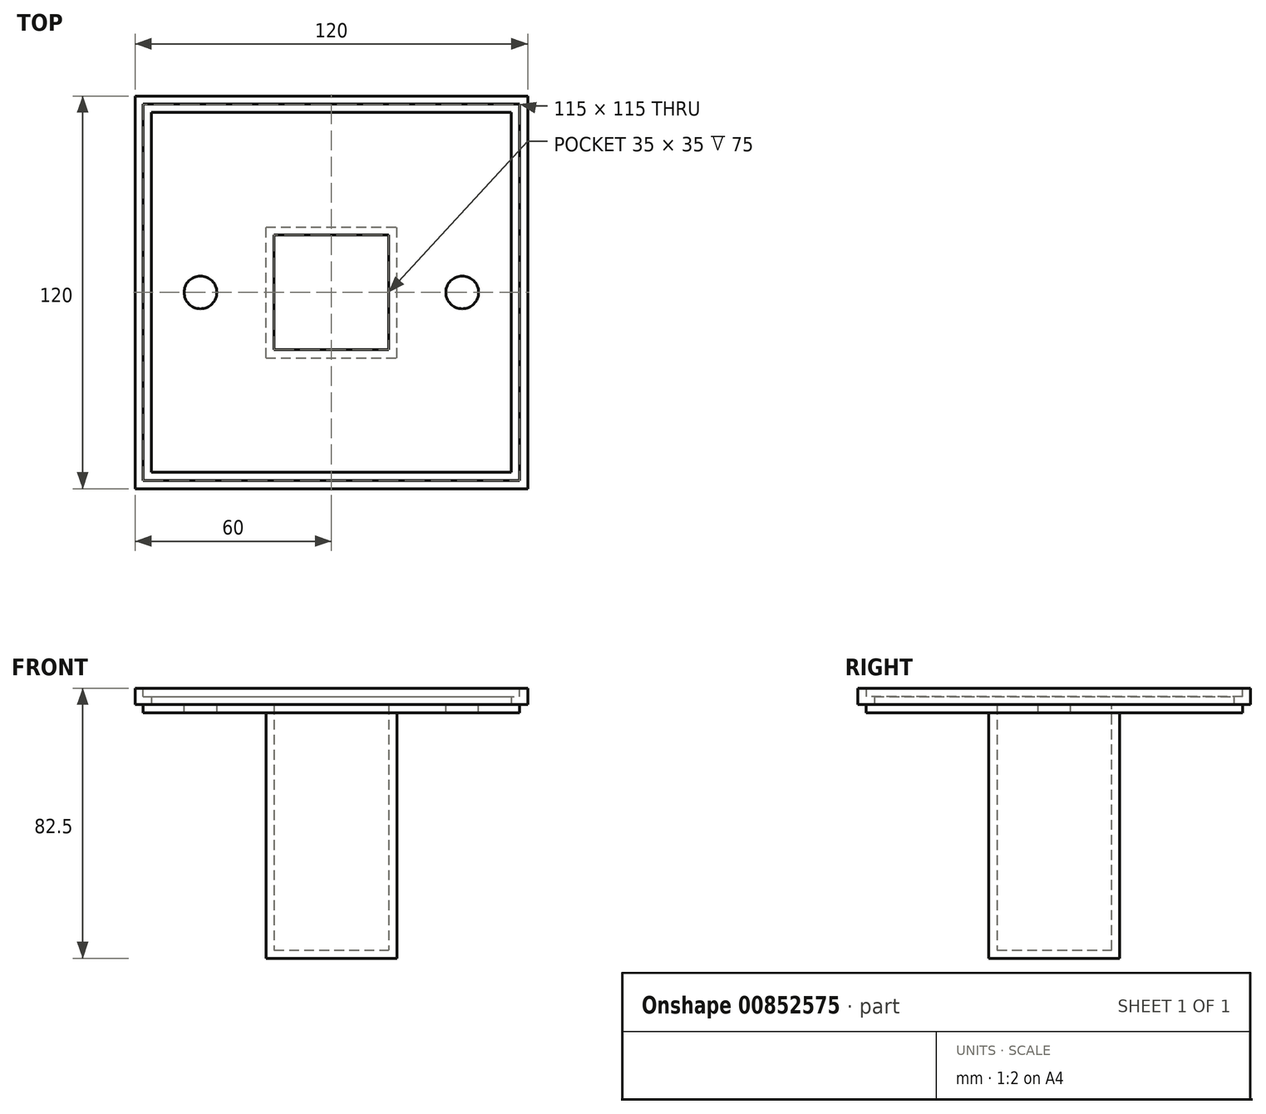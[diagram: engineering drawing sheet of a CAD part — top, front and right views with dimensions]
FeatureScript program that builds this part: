
annotation { "Feature Type Name" : "Feature", "Feature Type Description" : "" }
export const myFeature = defineFeature(function(context is Context, id is Id, definition is map)
    precondition{}
    {
        {
            var Q0;
            Q0=qCreatedBy(makeId("Top.planeOp"),FACE);
            cPlane(context, id + "F0", {"entities" : qUnion([Q0]), "cplaneType" : CPlaneType.OFFSET, "offset" : 75 * mm, "oppositeDirection" : true, "width" : 150 * mm, "height" : 150 * mm});
        }
        {
            var Q0;
            Q0=qCreatedBy(id+"F0.planeOp",FACE);
            var sketch = newSketch(context, id + "F1", { "sketchPlane" : qUnion([Q0])});
            skLineSegment(sketch, "E0.bottom", {"start": v(-20, -20) * mm, "end": v(20, -20) * mm});
            skLineSegment(sketch, "E0.top", {"start": v(-20, 20) * mm, "end": v(20, 20) * mm});
            skLineSegment(sketch, "E0.left", {"start": v(-20, -20) * mm, "end": v(-20, 20) * mm});
            skLineSegment(sketch, "E0.right", {"start": v(20, -20) * mm, "end": v(20, 20) * mm});
            skPoint(sketch, "E0.middle", {"position": v(0, 0) * mm});
            skSolve(sketch);
        }
        {
            var Q0;
            Q0=qCreatedBy(makeId("Top.planeOp"),FACE);
            cPlane(context, id + "F2", {"entities" : qUnion([Q0]), "cplaneType" : CPlaneType.OFFSET, "offset" : 2.5 * mm, "width" : 150 * mm, "height" : 150 * mm});
        }
        {
            var Q0;
            Q0=qCreatedBy(id+"F2.planeOp",FACE);
            cPlane(context, id + "F3", {"entities" : qUnion([Q0]), "cplaneType" : CPlaneType.OFFSET, "offset" : 2.5 * mm, "width" : 150 * mm, "height" : 150 * mm});
        }
        {
            var Q0;
            Q0=qCreatedBy(makeId("Top.planeOp"),FACE);
            var sketch = newSketch(context, id + "F4", { "sketchPlane" : qUnion([Q0])});
            skLineSegment(sketch, "E1.bottom", {"start": v(-57.5, -57.5) * mm, "end": v(57.5, -57.5) * mm});
            skLineSegment(sketch, "E1.top", {"start": v(-57.5, 57.5) * mm, "end": v(57.5, 57.5) * mm});
            skLineSegment(sketch, "E1.left", {"start": v(-57.5, -57.5) * mm, "end": v(-57.5, 57.5) * mm});
            skLineSegment(sketch, "E1.right", {"start": v(57.5, -57.5) * mm, "end": v(57.5, 57.5) * mm});
            skPoint(sketch, "E1.middle", {"position": v(0, 0) * mm});
            skSolve(sketch);
        }
        {
            var Q0;
            Q0=qCreatedBy(id+"F2.planeOp",FACE);
            var sketch = newSketch(context, id + "F5", { "sketchPlane" : qUnion([Q0])});
            skLineSegment(sketch, "E2.bottom", {"start": v(-57.5, -57.5) * mm, "end": v(57.5, -57.5) * mm});
            skLineSegment(sketch, "E2.top", {"start": v(-57.5, 57.5) * mm, "end": v(57.5, 57.5) * mm});
            skLineSegment(sketch, "E2.left", {"start": v(-57.5, -57.5) * mm, "end": v(-57.5, 57.5) * mm});
            skLineSegment(sketch, "E2.right", {"start": v(57.5, -57.5) * mm, "end": v(57.5, 57.5) * mm});
            skPoint(sketch, "E2.middle", {"position": v(0, 0) * mm});
            skSolve(sketch);
        }
        {
            var Q0;
            Q0=qCreatedBy(id+"F3.planeOp",FACE);
            var sketch = newSketch(context, id + "F6", { "sketchPlane" : qUnion([Q0])});
            skLineSegment(sketch, "E3.bottom", {"start": v(-60, 60) * mm, "end": v(60, 60) * mm});
            skLineSegment(sketch, "E3.top", {"start": v(-60, -60) * mm, "end": v(60, -60) * mm});
            skLineSegment(sketch, "E3.left", {"start": v(-60, 60) * mm, "end": v(-60, -60) * mm});
            skLineSegment(sketch, "E3.right", {"start": v(60, 60) * mm, "end": v(60, -60) * mm});
            skPoint(sketch, "E3.middle", {"position": v(0, 0) * mm});
            skSolve(sketch);
        }
        {
            var Q0;
            Q0=qCreatedBy(makeId("Top.planeOp"),FACE);
            var sketch = newSketch(context, id + "F7", { "sketchPlane" : qUnion([Q0])});
            skLineSegment(sketch, "E4.bottom", {"start": v(-20, -20) * mm, "end": v(20, -20) * mm});
            skLineSegment(sketch, "E4.top", {"start": v(-20, 20) * mm, "end": v(20, 20) * mm});
            skLineSegment(sketch, "E4.left", {"start": v(-20, -20) * mm, "end": v(-20, 20) * mm});
            skLineSegment(sketch, "E4.right", {"start": v(20, -20) * mm, "end": v(20, 20) * mm});
            skPoint(sketch, "E4.middle", {"position": v(0, 0) * mm});
            skSolve(sketch);
        }
        {
            var Q0;
            Q0=makeQuery(id+"F1.imprint","IMPRINT",FACE,{"disambiguationData":[TD([[makeQuery(id+"F1.imprint","IMPRINT",EDGE,{"derivedFrom":sQuery(id+"F1.wireOp",EDGE,"E0.bottom")}),1.0]])]});
            var Q1;
            Q1=makeQuery(id+"F7.imprint","IMPRINT",FACE,{"disambiguationData":[TD([[makeQuery(id+"F7.imprint","IMPRINT",EDGE,{"derivedFrom":sQuery(id+"F7.wireOp",EDGE,"E4.bottom")}),1.0]])]});
            loft(context, id + "F8", {"sheetProfilesArray" : [{ "sheetProfileEntities" : qUnion([Q0]) }, { "sheetProfileEntities" : qUnion([Q1]) }]});
        }
        {
            var Q1;
            Q1=makeQuery(id+"F4.imprint","IMPRINT",FACE,{"disambiguationData":[TD([[makeQuery(id+"F4.imprint","IMPRINT",EDGE,{"derivedFrom":sQuery(id+"F4.wireOp",EDGE,"E1.bottom")}),1.0]])]});
            var Q2;
            Q2=makeQuery(id+"F5.imprint","IMPRINT",FACE,{"disambiguationData":[TD([[makeQuery(id+"F5.imprint","IMPRINT",EDGE,{"derivedFrom":sQuery(id+"F5.wireOp",EDGE,"E2.bottom")}),1.0]])]});
            loft(context, id + "F9", {"operationType" : NewBodyOperationType.ADD, "sheetProfilesArray" : [{ "sheetProfileEntities" : qUnion([Q1]) }, { "sheetProfileEntities" : qUnion([Q2]) }]});
        }
        {
            var Q0;
            Q0=qCreatedBy(id+"F2.planeOp",FACE);
            var sketch = newSketch(context, id + "F10", { "sketchPlane" : qUnion([Q0])});
            skLineSegment(sketch, "E5.bottom", {"start": v(-60, 60) * mm, "end": v(60, 60) * mm});
            skLineSegment(sketch, "E5.top", {"start": v(-60, -60) * mm, "end": v(60, -60) * mm});
            skLineSegment(sketch, "E5.left", {"start": v(-60, 60) * mm, "end": v(-60, -60) * mm});
            skLineSegment(sketch, "E5.right", {"start": v(60, 60) * mm, "end": v(60, -60) * mm});
            skPoint(sketch, "E5.middle", {"position": v(0, 0) * mm});
            skSolve(sketch);
        }
        {
            var Q1;
            Q1=makeQuery(id+"F6.imprint","IMPRINT",FACE,{"disambiguationData":[TD([[makeQuery(id+"F6.imprint","IMPRINT",EDGE,{"derivedFrom":sQuery(id+"F6.wireOp",EDGE,"E3.bottom")}),-1.0]])]});
            var Q2;
            Q2=makeQuery(id+"F10.imprint","IMPRINT",FACE,{"disambiguationData":[TD([[makeQuery(id+"F10.imprint","IMPRINT",EDGE,{"derivedFrom":sQuery(id+"F10.wireOp",EDGE,"E5.bottom")}),-1.0]])]});
            loft(context, id + "F11", {"operationType" : NewBodyOperationType.ADD, "sheetProfilesArray" : [{ "sheetProfileEntities" : qUnion([Q1]) }, { "sheetProfileEntities" : qUnion([Q2]) }]});
        }
        {
            var Q0;
            Q0=makeQuery(id+"F11.opLoft","CAP_FACE",FACE,{"disambiguationData":[OSD([makeQuery(id+"F6.imprint","IMPRINT",FACE,{"disambiguationData":[TD([[makeQuery(id+"F6.imprint","IMPRINT",EDGE,{"derivedFrom":sQuery(id+"F6.wireOp",EDGE,"E3.bottom")}),-1.0]])]})])],"isStart":true});
            var sketch = newSketch(context, id + "F12", { "sketchPlane" : qUnion([Q0])});
            skPoint(sketch, "E6", {"position": v(0, 0) * mm});
            skSolve(sketch);
        }
        {
            var Q0;
            Q0=qCreatedBy(id+"F3.planeOp",FACE);
            cPlane(context, id + "F13", {"entities" : qUnion([Q0]), "cplaneType" : CPlaneType.OFFSET, "offset" : 2.5 * mm, "width" : 150 * mm, "height" : 150 * mm});
        }
        {
            var Q0;
            Q0=qCreatedBy(id+"F13.planeOp",FACE);
            var sketch = newSketch(context, id + "F14", { "sketchPlane" : qUnion([Q0])});
            skLineSegment(sketch, "E7.bottom", {"start": v(-60, 60) * mm, "end": v(60, 60) * mm});
            skLineSegment(sketch, "E7.top", {"start": v(-60, -60) * mm, "end": v(60, -60) * mm});
            skLineSegment(sketch, "E7.left", {"start": v(-60, 60) * mm, "end": v(-60, -60) * mm});
            skLineSegment(sketch, "E7.right", {"start": v(60, 60) * mm, "end": v(60, -60) * mm});
            skPoint(sketch, "E7.middle", {"position": v(0, 0) * mm});
            skSolve(sketch);
        }
        {
            var Q1;
            Q1=makeQuery(id+"F14.imprint","IMPRINT",FACE,{"disambiguationData":[TD([[makeQuery(id+"F14.imprint","IMPRINT",EDGE,{"derivedFrom":sQuery(id+"F14.wireOp",EDGE,"E7.bottom")}),-1.0]])]});
            var Q2;
            {var subQ0=sQuery(id+"F6.wireOp",EDGE,"E3.right");var subQ1=sQuery(id+"F6.wireOp",EDGE,"E3.left");var subQ2=sQuery(id+"F6.wireOp",EDGE,"E3.bottom");Q2=makeQuery(id+"F12.imprint","IMPRINT",FACE,{"disambiguationData":[TD([[makeQuery(id+"F12.imprint","IMPRINT",EDGE,{"derivedFrom":makeQuery(id+"F11.opLoft","MID_CAP_EDGE",EDGE,{"disambiguationData":[OSD([subQ2,subQ1,subQ0])],"capPos":0.0})}),-1.0]])]});}
            loft(context, id + "F15", {"operationType" : NewBodyOperationType.ADD, "sheetProfilesArray" : [{ "sheetProfileEntities" : qUnion([Q1]) }, { "sheetProfileEntities" : qUnion([Q2]) }]});
        }
        {
            var Q0;
            Q0=makeQuery(id+"F15.opLoft","CAP_FACE",FACE,{"disambiguationData":[OSD([makeQuery(id+"F14.imprint","IMPRINT",FACE,{"disambiguationData":[TD([[makeQuery(id+"F14.imprint","IMPRINT",EDGE,{"derivedFrom":sQuery(id+"F14.wireOp",EDGE,"E7.bottom")}),-1.0]])]})])],"isStart":true});
            shell(context, id + "F16", {"entities" : qUnion([Q0]), "thickness" : 2.5 * mm});
        }
        {
            var Q0;
            Q0=makeQuery(id+"F16.opShell","OFFSET_FACE",FACE,{"disambiguationData":[OSD([makeQuery(id+"F4.imprint","IMPRINT",FACE,{"disambiguationData":[TD([[makeQuery(id+"F4.imprint","IMPRINT",EDGE,{"derivedFrom":sQuery(id+"F4.wireOp",EDGE,"E1.bottom")}),1.0]])]})])]});
            var sketch = newSketch(context, id + "F17", { "sketchPlane" : qUnion([Q0])});
            skPoint(sketch, "E8", {"position": v(-40, 0) * mm});
            skPoint(sketch, "E9", {"position": v(40, 0) * mm});
            skSolve(sketch);
        }
        {
            var Q0;
            Q0=sQuery(id+"F17.wireOp",VERTEX,"E8");
            var Q1;
            Q1=makeQuery(id+"F8.opLoft","SWEPT_BODY",BODY,{"disambiguationData":[OSD([makeQuery(id+"F1.imprint","IMPRINT",FACE,{"disambiguationData":[TD([[makeQuery(id+"F1.imprint","IMPRINT",EDGE,{"derivedFrom":sQuery(id+"F1.wireOp",EDGE,"E0.bottom")}),1.0]])]}),makeQuery(id+"F7.imprint","IMPRINT",FACE,{"disambiguationData":[TD([[makeQuery(id+"F7.imprint","IMPRINT",EDGE,{"derivedFrom":sQuery(id+"F7.wireOp",EDGE,"E4.bottom")}),1.0]])]})])]});
            hole(context, id + "F18", {"style" : HoleStyle.SIMPLE, "endStyle" : HoleEndStyle.THROUGH, "holeDiameter" : 10 * mm, "majorDiameter" : 5 * mm, "isTappedThrough" : true, "tappedDepth" : 12 * mm, "tapClearance" : 3, "locations" : qUnion([Q0]), "scope" : qUnion([Q1])});
        }
        {
            var Q0;
            Q0=makeQuery(id+"F16.opShell","OFFSET_FACE",FACE,{"disambiguationData":[OSD([makeQuery(id+"F4.imprint","IMPRINT",FACE,{"disambiguationData":[TD([[makeQuery(id+"F4.imprint","IMPRINT",EDGE,{"derivedFrom":sQuery(id+"F4.wireOp",EDGE,"E1.bottom")}),1.0]])]})])]});
            var sketch = newSketch(context, id + "F19", { "sketchPlane" : qUnion([Q0])});
            skPoint(sketch, "E10", {"position": v(40, 0) * mm});
            skSolve(sketch);
        }
        {
            var Q0;
            Q0=sQuery(id+"F19.wireOp",VERTEX,"E10");
            var Q1;
            Q1=makeQuery(id+"F8.opLoft","SWEPT_BODY",BODY,{"disambiguationData":[OSD([makeQuery(id+"F1.imprint","IMPRINT",FACE,{"disambiguationData":[TD([[makeQuery(id+"F1.imprint","IMPRINT",EDGE,{"derivedFrom":sQuery(id+"F1.wireOp",EDGE,"E0.bottom")}),1.0]])]}),makeQuery(id+"F7.imprint","IMPRINT",FACE,{"disambiguationData":[TD([[makeQuery(id+"F7.imprint","IMPRINT",EDGE,{"derivedFrom":sQuery(id+"F7.wireOp",EDGE,"E4.bottom")}),1.0]])]})])]});
            hole(context, id + "F20", {"style" : HoleStyle.SIMPLE, "endStyle" : HoleEndStyle.THROUGH, "holeDiameter" : 10 * mm, "majorDiameter" : 5 * mm, "isTappedThrough" : true, "tappedDepth" : 12 * mm, "tapClearance" : 3, "locations" : qUnion([Q0]), "scope" : qUnion([Q1])});
        }
    });
